# Revit family: Haworth_BuzziShade_Light
name_source: partatom
category: Lighting Fixtures
revit_build: Autodesk Revit 2018 (Build: 20170223_1515(x64)
units: mm (PartAtom-declared; Revit-internal decimal feet)

## family parameters
Cut with Voids When Loaded = No
Host = Face
Light Source = Yes
Part Type = Normal
Room Calculation Point = No
Round Connector Dimension = Use Diameter
Shared = No

## types (2) — shared parameters
Assembly Code = E2020200
Color Filter = 16777215
Dimming Lamp Color Temperature Shift = <None>
Emit Shape Visible in Rendering = No
Emit from Circle Diameter = 24 "
Manufacturer = Haworth
Max. Cable Length = 196.85 "
Min. Cable Length = 10 "
Model = HCBZ-SHP
Note = Verify Final Dim. w/ Haworth
Photometric Web File = generic
Revision = 1
URL = http://www.haworth.com
URL - Product = https://www.haworth.com
Warranty = http://www.haworth.com
zero-valued in all types: Default Elevation

## per-type parameters (varying)
| type | Actual Depth | Actual Height | Actual Width | Description | Large | Medium | Tilt Angle |
| HCBZ-SHP2 - Large | 44.09 " | 24.41 " | 44.09 " | Haworth BuzziShade Pendant Light Large | Yes | No | 90.00° |
| HCBZ-SHP1 - Medium | 29.13 " | 16.54 " | 29.13 " | Haworth BuzziShade Pendant Light Medium | No | Yes | 60.00° |

## geometry (parser evidence)
native form markers: Sweep x5
no freeform markers — native parametric forms only
